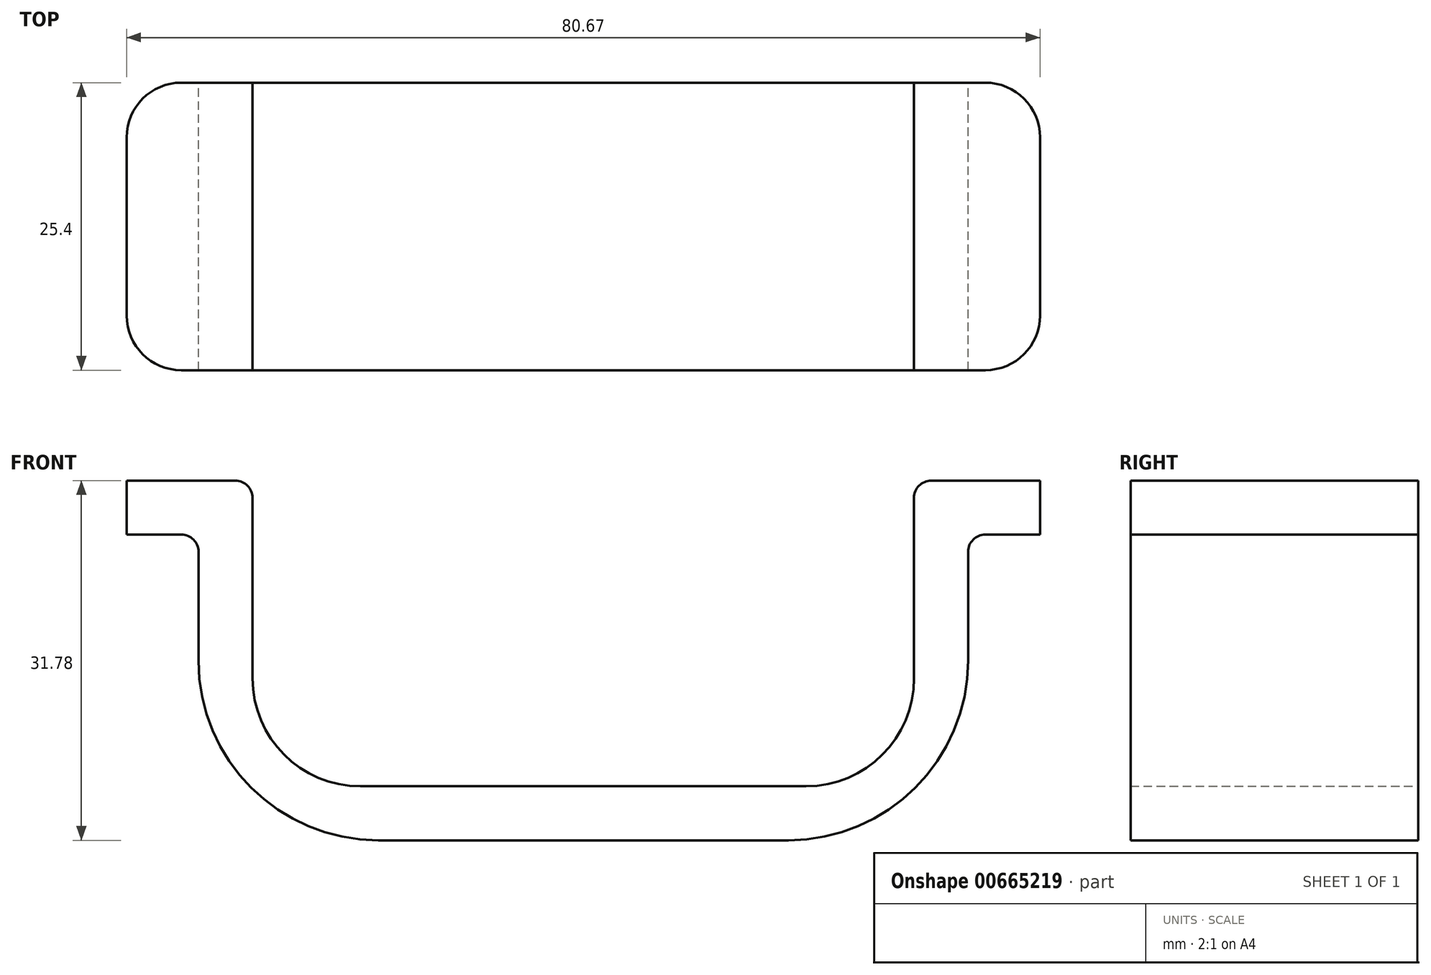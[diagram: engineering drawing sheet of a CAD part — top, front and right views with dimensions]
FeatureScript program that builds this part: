
annotation { "Feature Type Name" : "Feature", "Feature Type Description" : "" }
export const myFeature = defineFeature(function(context is Context, id is Id, definition is map)
    precondition{}
    {
        {
            var Q0;
            Q0=qCreatedBy(makeId("Front.planeOp"),FACE);
            var sketch = newSketch(context, id + "F0", { "sketchPlane" : qUnion([Q0])});
            skLineSegment(sketch, "E0.bottom", {"start": v(0, 0) * mm, "end": v(67.97, 0) * mm});
            skLineSegment(sketch, "E0.top", {"start": v(14.3, 4.78) * mm, "end": v(53.67, 4.78) * mm});
            skLineSegment(sketch, "E0.left", {"start": v(0, 0) * mm, "end": v(0, 4.78) * mm});
            skLineSegment(sketch, "E0.right", {"start": v(67.97, 0) * mm, "end": v(67.97, 4.78) * mm});
            skLineSegment(sketch, "E1.top", {"start": v(0, 31.78) * mm, "end": v(4.78, 31.78) * mm});
            skLineSegment(sketch, "E1.left", {"start": v(0, 4.78) * mm, "end": v(0, 27) * mm});
            skLineSegment(sketch, "E1.right", {"start": v(4.78, 14.3) * mm, "end": v(4.78, 31.78) * mm});
            skLineSegment(sketch, "E2.top", {"start": v(67.97, 31.78) * mm, "end": v(63.2, 31.78) * mm});
            skLineSegment(sketch, "E2.left", {"start": v(67.97, 4.78) * mm, "end": v(67.97, 27) * mm});
            skLineSegment(sketch, "E2.right", {"start": v(63.2, 14.3) * mm, "end": v(63.2, 31.78) * mm});
            skLineSegment(sketch, "E3.bottom", {"start": v(0, 31.78) * mm, "end": v(-6.35, 31.78) * mm});
            skLineSegment(sketch, "E3.top", {"start": v(0, 27) * mm, "end": v(-6.35, 27) * mm});
            skLineSegment(sketch, "E3.right", {"start": v(-6.35, 31.78) * mm, "end": v(-6.35, 27) * mm});
            skLineSegment(sketch, "E4.bottom", {"start": v(67.97, 31.78) * mm, "end": v(74.32, 31.78) * mm});
            skLineSegment(sketch, "E4.top", {"start": v(67.97, 27) * mm, "end": v(74.32, 27) * mm});
            skLineSegment(sketch, "E4.right", {"start": v(74.32, 31.78) * mm, "end": v(74.32, 27) * mm});
            skPoint(sketch, "E5.visualSharp", {"position": v(4.78, 4.78) * mm});
            skArc(sketch, "E5.filletArc", {"start": v(4.78, 14.3) * mm, "mid": v(7.57, 7.57) * mm, "end": v(14.3, 4.78) * mm});
            skPoint(sketch, "E6.visualSharp", {"position": v(63.2, 4.78) * mm});
            skArc(sketch, "E6.filletArc", {"start": v(53.67, 4.78) * mm, "mid": v(60.4, 7.57) * mm, "end": v(63.2, 14.3) * mm});
            skSolve(sketch);
        }
        {
            var Q0;
            Q0=makeQuery(id+"F0.imprint","IMPRINT",FACE,{"disambiguationData":[TD([[makeQuery(id+"F0.imprint","IMPRINT",EDGE,{"derivedFrom":sQuery(id+"F0.wireOp",EDGE,"E0.bottom")}),1.0]])]});
            extrude(context, id + "F1", {"entities" : qUnion([Q0]), "depth" : 25.4 * mm, "offsetDistance" : 25.4 * mm});
        }
        {
            var Q0;
            Q0=makeQuery(id+"F1.opExtrude","SWEPT_EDGE",EDGE,{"disambiguationData":[OSD([sQuery(id+"F0.wireOp",EDGE,"E0.bottom"),sQuery(id+"F0.wireOp",EDGE,"E0.left")])]});
            var Q1;
            Q1=makeQuery(id+"F1.opExtrude","SWEPT_EDGE",EDGE,{"disambiguationData":[OSD([sQuery(id+"F0.wireOp",EDGE,"E0.bottom"),sQuery(id+"F0.wireOp",EDGE,"E0.right")])]});
            fillet(context, id + "F2", {"entities" : qUnion([Q0, Q1]), "radius" : 15.88 * mm, "tangentPropagation" : true, "allowEdgeOverflow" : false});
        }
        {
            var Q0;
            Q0=makeQuery(id+"F1.opExtrude","CAP_EDGE",EDGE,{"disambiguationData":[OSD([sQuery(id+"F0.wireOp",EDGE,"E3.right")])],"isStart":true});
            var Q1;
            Q1=makeQuery(id+"F1.opExtrude","CAP_EDGE",EDGE,{"disambiguationData":[OSD([sQuery(id+"F0.wireOp",EDGE,"E3.right")])],"isStart":false});
            var Q2;
            Q2=makeQuery(id+"F1.opExtrude","CAP_EDGE",EDGE,{"disambiguationData":[OSD([sQuery(id+"F0.wireOp",EDGE,"E4.right")])],"isStart":true});
            var Q3;
            Q3=makeQuery(id+"F1.opExtrude","CAP_EDGE",EDGE,{"disambiguationData":[OSD([sQuery(id+"F0.wireOp",EDGE,"E4.right")])],"isStart":false});
            fillet(context, id + "F3", {"entities" : qUnion([Q0, Q1, Q2, Q3]), "radius" : 4.83 * mm, "tangentPropagation" : true, "allowEdgeOverflow" : false});
        }
        {
            var Q0;
            Q0=makeQuery(id+"F1.opExtrude","SWEPT_EDGE",EDGE,{"disambiguationData":[OSD([sQuery(id+"F0.wireOp",EDGE,"E1.left"),sQuery(id+"F0.wireOp",EDGE,"E3.top")])]});
            var Q1;
            Q1=makeQuery(id+"F1.opExtrude","SWEPT_EDGE",EDGE,{"disambiguationData":[OSD([sQuery(id+"F0.wireOp",EDGE,"E1.top"),sQuery(id+"F0.wireOp",EDGE,"E1.right")])]});
            var Q2;
            Q2=makeQuery(id+"F1.opExtrude","SWEPT_EDGE",EDGE,{"disambiguationData":[OSD([sQuery(id+"F0.wireOp",EDGE,"E2.top"),sQuery(id+"F0.wireOp",EDGE,"E2.right")])]});
            var Q3;
            Q3=makeQuery(id+"F1.opExtrude","SWEPT_EDGE",EDGE,{"disambiguationData":[OSD([sQuery(id+"F0.wireOp",EDGE,"E2.left"),sQuery(id+"F0.wireOp",EDGE,"E4.top")])]});
            fillet(context, id + "F4", {"entities" : qUnion([Q0, Q1, Q2, Q3]), "radius" : 1.52 * mm, "tangentPropagation" : true, "allowEdgeOverflow" : false});
        }
    });
